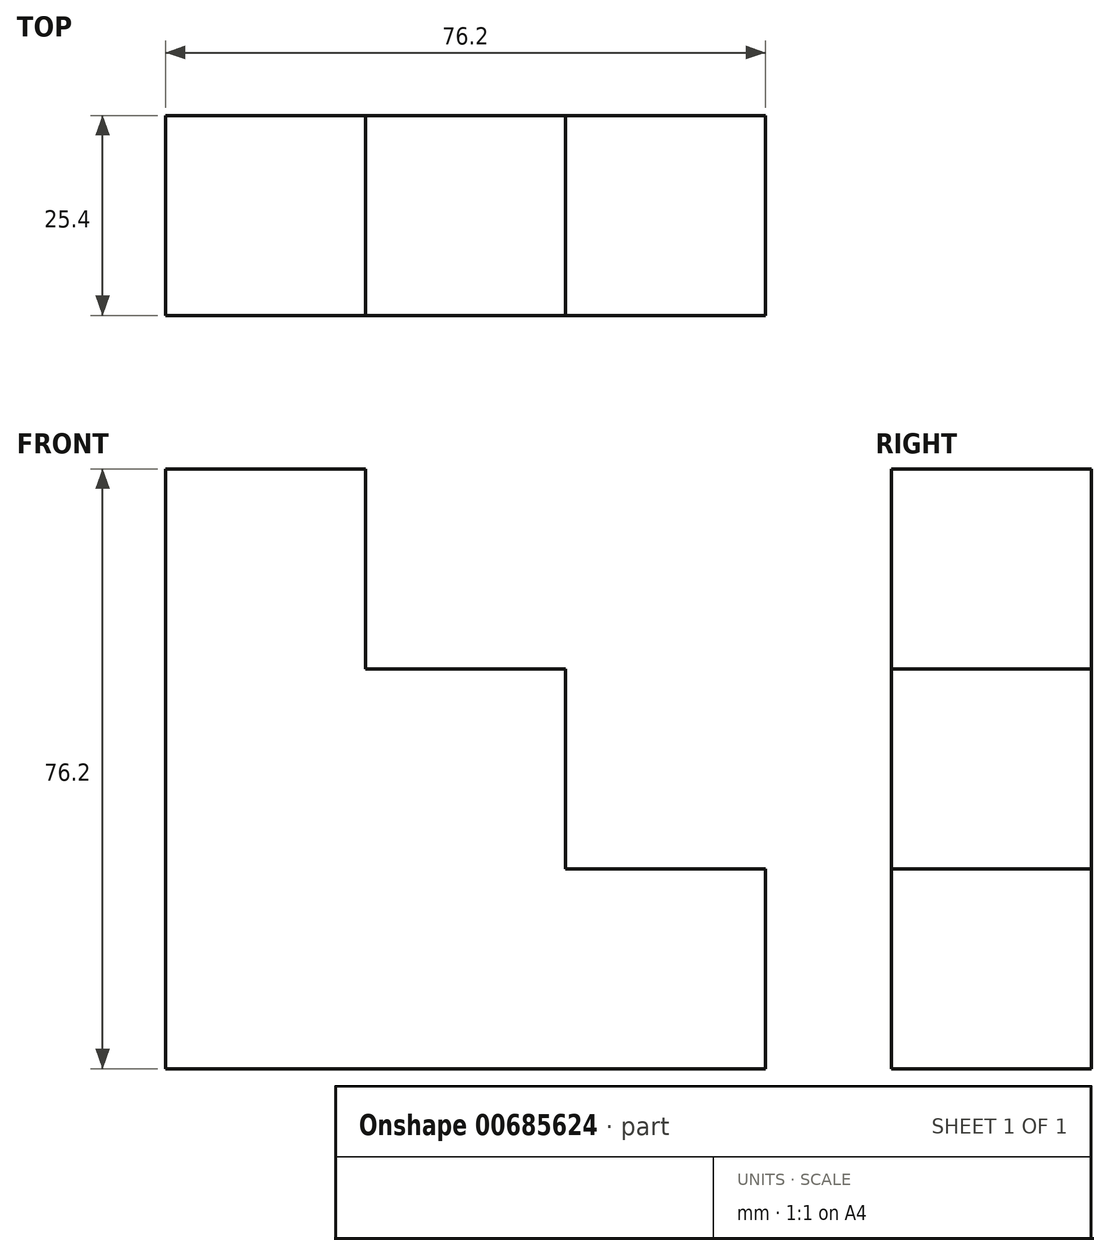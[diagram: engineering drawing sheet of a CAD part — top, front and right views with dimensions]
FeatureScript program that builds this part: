
annotation { "Feature Type Name" : "Feature", "Feature Type Description" : "" }
export const myFeature = defineFeature(function(context is Context, id is Id, definition is map)
    precondition{}
    {
        {
            var Q0;
            Q0=qCreatedBy(makeId("Front.planeOp"),FACE);
            var sketch = newSketch(context, id + "F0", { "sketchPlane" : qUnion([Q0])});
            skLineSegment(sketch, "E0", {"start": v(-62.5, 76.2) * mm, "end": v(-62.5, 0) * mm});
            skLineSegment(sketch, "E1", {"start": v(-62.5, 0) * mm, "end": v(13.7, 0) * mm});
            skLineSegment(sketch, "E2", {"start": v(13.7, 0) * mm, "end": v(13.7, 25.4) * mm});
            skLineSegment(sketch, "E3", {"start": v(13.7, 25.4) * mm, "end": v(-11.7, 25.4) * mm});
            skLineSegment(sketch, "E4", {"start": v(-11.7, 25.4) * mm, "end": v(-11.7, 50.8) * mm});
            skLineSegment(sketch, "E5", {"start": v(-11.7, 50.8) * mm, "end": v(-37.1, 50.8) * mm});
            skLineSegment(sketch, "E6", {"start": v(-37.1, 50.8) * mm, "end": v(-37.1, 76.2) * mm});
            skLineSegment(sketch, "E7", {"start": v(-37.1, 76.2) * mm, "end": v(-62.5, 76.2) * mm});
            skSolve(sketch);
        }
        {
            var Q0;
            Q0=makeQuery(id+"F0.imprint","IMPRINT",FACE,{"disambiguationData":[TD([[makeQuery(id+"F0.imprint","IMPRINT",EDGE,{"derivedFrom":sQuery(id+"F0.wireOp",EDGE,"E0")}),1.0]])]});
            extrude(context, id + "F1", {"entities" : qUnion([Q0]), "depth" : 25.4 * mm, "offsetDistance" : 25.4 * mm});
        }
    });
